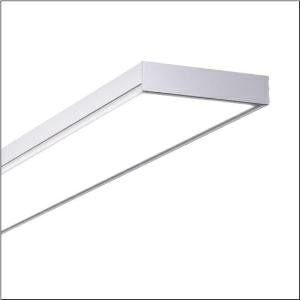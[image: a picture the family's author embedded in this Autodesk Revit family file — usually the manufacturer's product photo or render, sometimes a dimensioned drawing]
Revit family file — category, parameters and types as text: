
# Revit family: apollon_r__31_surface_51mp26wm2341e_8ded
name_source: partatom
category: Lighting Fixtures
units: mm (PartAtom-declared; Revit-internal decimal feet)

## family parameters
Cut with Voids When Loaded = No
Host = Face
Light Source = No
Part Type = Normal
Room Calculation Point = No
Round Connector Dimension = Use Diameter
Shared = No

## types (1)
- Apollon® 31 Surface (1 x LED, 4400 lm, 33 W, 3000K)
    Apparent Load = 33 VA
    CIE Flux Codes = 61 87 97 97 100
    Color Rendering = 80
    Color Temperature = 3000K
    Default Elevation = 1800 mm
    Description = Apollon® 31 Surface, office luminaire, primary optical cover: micro prismatic cover, of PMMA, light emission: direct distribution, primary light characteristic: symmetric, installation type: surface-mounted, LED, rated luminous flux: 4.400lm, luminous efficacy: 133lm/W, light colour: 830, colour temperature: 3000K, control gear: ECG Multilumen, with terminal, 3-pole, mains connection: 220..240V, AC, 50/60Hz, rated input power: 33W, housing, of sheet steel, coil coated, metallic grey (RAL 9006), length: 1.545mm, width: 200mm, height: 44mm, protection rating (complete): IP20, insulation class (complete): insulation class II (safety insulation), certification: CE, impact resistance: IK02, permissible operating ambient temperature: -20..+40°C, packaging unit: 1 piece
    Height = 44 mm
    Lamp = 1 x LED
    Lamp Light Flux = 4400 lm
    Lamp Power = 33 W
    Lamp count = 1
    Length = 1545 mm
    Luminous efficacy = 133 lm/W
    Manufacturer = Siteco
    ModVariant = No
    Model = 51MP26WM2341E
    Mounting Place = Ceiling
    Mounting Type = Surface mounted
    Number of Poles = 1
    OnlyDefault = Yes
    Power Factor = 1
    Product Name = Apollon® 31 Surface
    Product group = office luminaire | ceiling mounted
    ProductGroupID = 304
    Protection Class = Protection class II
    Protection Degree = IP 20
    RLX_Detail_Level = 1
    RLX_Emergency_Light_Flux = 0 lm
    RLX_Emergency_Type = 0
    RLX_Emergency_Type_DB = No
    RlxData = <blob elided: 24101 chars, md5=185c48db>
    Socket = socket
    Standby Power = 0 W
    System Light Flux = 4400 lm
    System Power = 33 W
    Type Comments = Product without accessories
    Type Image = l_1007091.jpg
    URL = http://relux.com
    VarID = ---
    Voltage = 0 V
    Weight = 0.00 kg
    Width = 200 mm  [stored 0.656168 ft]

note: [stored X ft] marks values corroborated as IEEE doubles in the binary element streams (Revit-internal decimal feet)

## geometry (parser evidence)
native form markers: Blend x4, Sweep x11
no freeform markers — native parametric forms only
